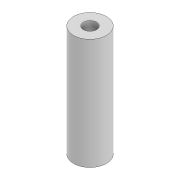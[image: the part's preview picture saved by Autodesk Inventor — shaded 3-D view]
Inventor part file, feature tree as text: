
AUTODESK INVENTOR PART (.ipt)
format: ipt  version: 2022 (Build 260153000, 153)  size: 81,920 bytes
history: native  units: mm
features: extrude x1, sketch x1
ambient origin geometry x8: Origin, YZ Plane, XZ Plane, XY Plane, X Axis, Y Axis, Z Axis, Center Point
bodies: Solid1 (feature_tree)
feature tree (2):
  extrude  "Extrusion1"  Depth=27.0mm
  sketch  "Sketch1"  dims[d0=3.2mm d1=8.0mm d2=27.0mm d3=0.0mm]
